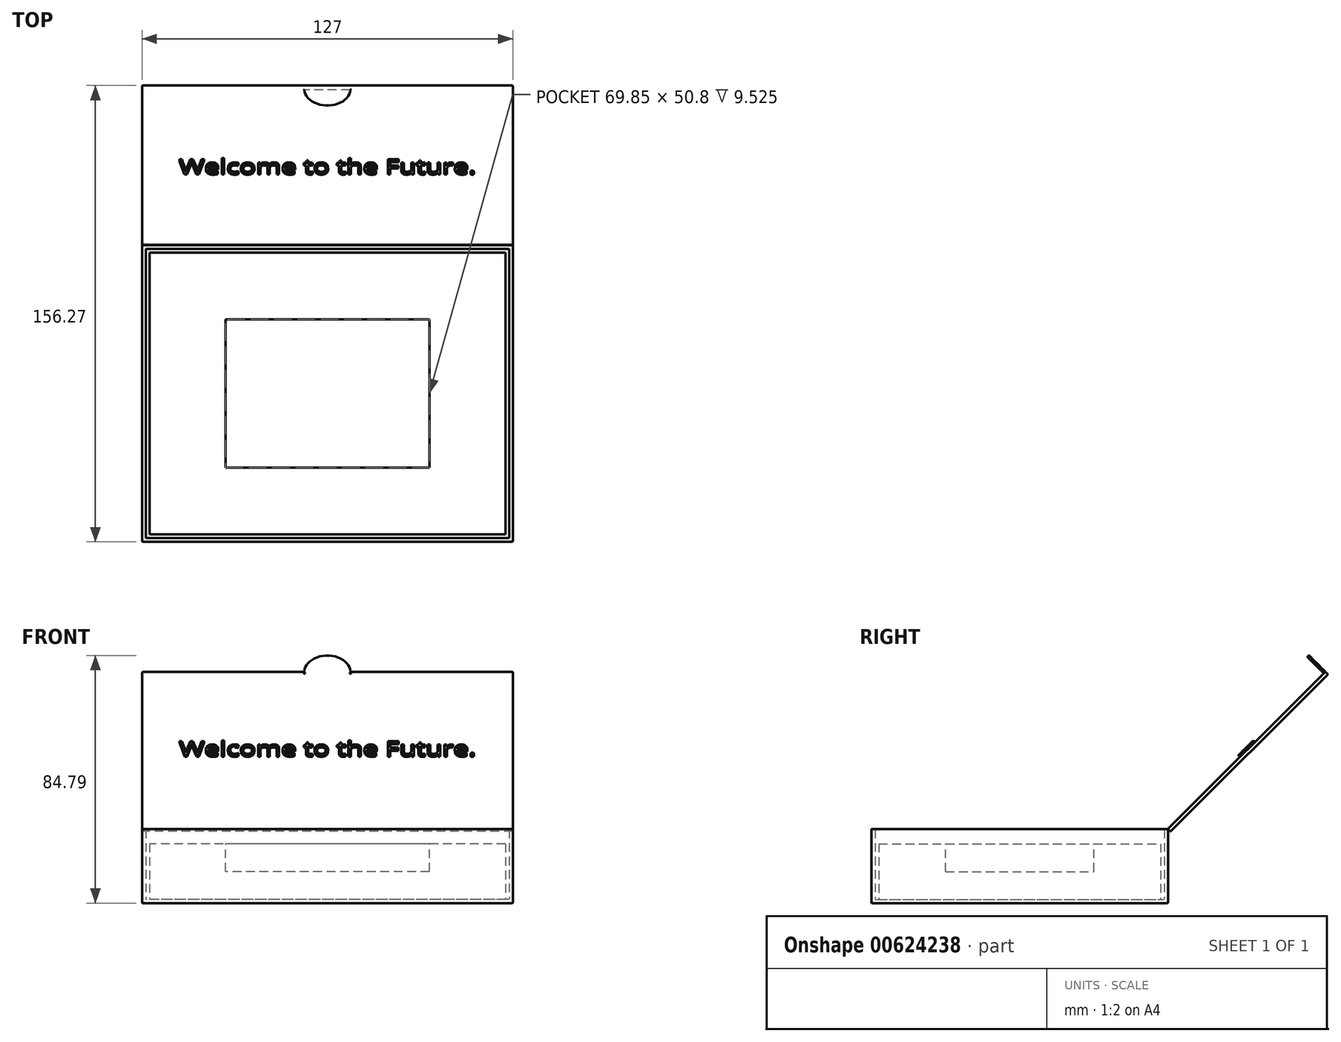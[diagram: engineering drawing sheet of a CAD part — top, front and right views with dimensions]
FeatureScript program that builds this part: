
annotation { "Feature Type Name" : "Feature", "Feature Type Description" : "" }
export const myFeature = defineFeature(function(context is Context, id is Id, definition is map)
    precondition{}
    {
        {
            var Q0;
            Q0=qCreatedBy(makeId("Top.planeOp"),FACE);
            var sketch = newSketch(context, id + "F0", { "sketchPlane" : qUnion([Q0])});
            skLineSegment(sketch, "E0.bottom", {"start": v(63.5, -50.8) * mm, "end": v(-63.5, -50.8) * mm});
            skLineSegment(sketch, "E0.top", {"start": v(63.5, 50.8) * mm, "end": v(-63.5, 50.8) * mm});
            skLineSegment(sketch, "E0.left", {"start": v(63.5, -50.8) * mm, "end": v(63.5, 50.8) * mm});
            skLineSegment(sketch, "E0.right", {"start": v(-63.5, -50.8) * mm, "end": v(-63.5, 50.8) * mm});
            skPoint(sketch, "E0.middle", {"position": v(0, 0) * mm});
            skSolve(sketch);
        }
        {
            var Q0;
            Q0 = qSketchRegion(id + "F0", true);
            extrude(context, id + "F1", {"entities" : qUnion([Q0]), "depth" : 25.4 * mm, "offsetDistance" : 25.4 * mm});
        }
        {
            var Q0;
            Q0=makeQuery(id+"F1.opExtrude","CAP_FACE",FACE,{"disambiguationData":[OSD([sQuery(id+"F0.wireOp",EDGE,"E0.bottom"),sQuery(id+"F0.wireOp",EDGE,"E0.top"),sQuery(id+"F0.wireOp",EDGE,"E0.left"),sQuery(id+"F0.wireOp",EDGE,"E0.right")])],"isStart":false});
            shell(context, id + "F2", {"entities" : qUnion([Q0]), "thickness" : 1.27 * mm});
        }
        {
            var Q0;
            Q0=qCreatedBy(makeId("Right.planeOp"),FACE);
            var sketch = newSketch(context, id + "F3", { "sketchPlane" : qUnion([Q0])});
            skLineSegment(sketch, "E1.0.2", {"start": v(50.8, 25.4) * mm, "end": v(-50.8, 25.4) * mm, "construction": true});
            skLineSegment(sketch, "E2", {"start": v(50.8, 25.4) * mm, "end": v(104.68, 79.28) * mm});
            skLineSegment(sketch, "E3.0", {"start": v(51.7, 24.5) * mm, "end": v(105.58, 78.38) * mm});
            skLineSegment(sketch, "E4", {"start": v(50.8, 25.4) * mm, "end": v(51.7, 24.5) * mm});
            skLineSegment(sketch, "E5", {"start": v(104.68, 79.28) * mm, "end": v(105.58, 78.38) * mm});
            skSolve(sketch);
        }
        {
            var Q0;
            Q0 = qSketchRegion(id + "F3", true);
            var Q1;
            Q1=makeQuery(id+"F1.opExtrude","SWEPT_FACE",FACE,{"disambiguationData":[OSD([sQuery(id+"F0.wireOp",EDGE,"E0.left")])]});
            var Q2;
            Q2=makeQuery(id+"F1.opExtrude","SWEPT_FACE",FACE,{"disambiguationData":[OSD([sQuery(id+"F0.wireOp",EDGE,"E0.right")])]});
            extrude(context, id + "F4", {"entities" : qUnion([Q0]), "endBound" : BoundingType.UP_TO_SURFACE, "depth" : 25.4 * mm, "endBoundEntityFace" : qUnion([Q1]), "offsetDistance" : 25.4 * mm, "hasSecondDirection" : true, "secondDirectionBound" : SecondDirectionBoundingType.UP_TO_SURFACE, "secondDirectionOppositeDirection" : true, "secondDirectionDepth" : 25.4 * mm, "secondDirectionBoundEntityFace" : qUnion([Q2])});
        }
        {
            var Q0;
            Q0=makeQuery(id+"F1.opExtrude","SWEPT_EDGE",EDGE,{"disambiguationData":[OSD([sQuery(id+"F0.wireOp",EDGE,"E0.bottom"),sQuery(id+"F0.wireOp",EDGE,"E0.left")])]});
            var Q1;
            Q1=makeQuery(id+"F1.opExtrude","SWEPT_EDGE",EDGE,{"disambiguationData":[OSD([sQuery(id+"F0.wireOp",EDGE,"E0.bottom"),sQuery(id+"F0.wireOp",EDGE,"E0.right")])]});
            var Q2;
            Q2=makeQuery(id+"F1.opExtrude","CAP_FACE",FACE,{"disambiguationData":[OSD([sQuery(id+"F0.wireOp",EDGE,"E0.bottom"),sQuery(id+"F0.wireOp",EDGE,"E0.top"),sQuery(id+"F0.wireOp",EDGE,"E0.left"),sQuery(id+"F0.wireOp",EDGE,"E0.right")])],"isStart":true});
            var Q3;
            Q3=makeQuery(id+"F2.opShell","OFFSET_FACE",FACE,{"disambiguationData":[OSD([sQuery(id+"F0.wireOp",EDGE,"E0.bottom"),sQuery(id+"F0.wireOp",EDGE,"E0.top"),sQuery(id+"F0.wireOp",EDGE,"E0.left"),sQuery(id+"F0.wireOp",EDGE,"E0.right")])]});
            var Q4;
            Q4=makeQuery(id+"F2.opShell","OFFSET_FACE",FACE,{"disambiguationData":[OSD([sQuery(id+"F0.wireOp",EDGE,"E0.bottom")])]});
            var Q5;
            Q5=makeQuery(id+"F2.opShell","OFFSET_FACE",FACE,{"disambiguationData":[OSD([sQuery(id+"F0.wireOp",EDGE,"E0.top")])]});
            var Q6;
            Q6=makeQuery(id+"F1.opExtrude","CAP_FACE",FACE,{"disambiguationData":[OSD([sQuery(id+"F0.wireOp",EDGE,"E0.bottom"),sQuery(id+"F0.wireOp",EDGE,"E0.top"),sQuery(id+"F0.wireOp",EDGE,"E0.left"),sQuery(id+"F0.wireOp",EDGE,"E0.right")])],"isStart":false});
            fillet(context, id + "F5", {"entities" : qUnion([Q0, Q1, Q2, Q3, Q4, Q5, Q6]), "radius" : 0.25 * mm, "tangentPropagation" : true, "allowEdgeOverflow" : false});
        }
        {
            var Q0;
            Q0=makeQuery(id+"F4.opExtrude","SWEPT_FACE",FACE,{"disambiguationData":[OSD([sQuery(id+"F3.wireOp",EDGE,"E5")])]});
            var sketch = newSketch(context, id + "F6", { "sketchPlane" : qUnion([Q0])});
            skArc(sketch, "E6", {"start": v(7.94, -17.96) * mm, "mid": v(0, -10.02) * mm, "end": v(-7.94, -17.96) * mm});
            skLineSegment(sketch, "E7", {"start": v(-7.94, -17.96) * mm, "end": v(7.94, -17.96) * mm});
            skSolve(sketch);
        }
        {
            var Q0;
            Q0 = qSketchRegion(id + "F6", true);
            extrude(context, id + "F7", {"entities" : qUnion([Q0]), "operationType" : NewBodyOperationType.ADD, "oppositeDirection" : true, "depth" : 0.76 * mm, "offsetDistance" : 25.4 * mm});
        }
        {
            var Q0;
            Q0=makeQuery(id+"F4.opExtrude","SWEPT_FACE",FACE,{"disambiguationData":[OSD([sQuery(id+"F3.wireOp",EDGE,"E3.0")])]});
            var Q1;
            Q1=makeQuery(id+"F4.opExtrude","SWEPT_FACE",FACE,{"disambiguationData":[OSD([sQuery(id+"F3.wireOp",EDGE,"E2")])]});
            var Q2;
            Q2=makeQuery(id+"F4.opExtrude","SWEPT_FACE",FACE,{"disambiguationData":[OSD([sQuery(id+"F3.wireOp",EDGE,"E5")])]});
            var Q3;
            Q3=makeQuery(id+"F7.opExtrude","CAP_EDGE",EDGE,{"disambiguationData":[OSD([sQuery(id+"F6.wireOp",EDGE,"E6")])],"isStart":false});
            fillet(context, id + "F8", {"entities" : qUnion([Q0, Q1, Q2, Q3]), "radius" : 0.25 * mm, "tangentPropagation" : true, "allowEdgeOverflow" : false});
        }
        {
            var Q0;
            Q0=makeQuery(id+"F4.opExtrude","SWEPT_FACE",FACE,{"disambiguationData":[OSD([sQuery(id+"F3.wireOp",EDGE,"E2")])]});
            var sketch = newSketch(context, id + "F9", { "sketchPlane" : qUnion([Q0])});
            skPoint(sketch, "E8", {"position": v(-63.25, 91.98) * mm});
            skPoint(sketch, "E9", {"position": v(0, 130.08) * mm});
            skText(sketch, "E10", { "text": "Welcome to the Future.", "fontName": "OpenSans-Regular.ttf"});
            const initialGuessF9  = {"E10": [-0.0508, 0.08892, 1, 0, 0.00671]};
            skSetInitialGuess(sketch, initialGuessF9);
            skSolve(sketch);
        }
        {
            var Q0;
            Q0=makeQuery(id+"F2.opShell","OFFSET_FACE",FACE,{"disambiguationData":[OSD([sQuery(id+"F0.wireOp",EDGE,"E0.bottom"),sQuery(id+"F0.wireOp",EDGE,"E0.top"),sQuery(id+"F0.wireOp",EDGE,"E0.left"),sQuery(id+"F0.wireOp",EDGE,"E0.right")])]});
            var sketch = newSketch(context, id + "F10", { "sketchPlane" : qUnion([Q0])});
            skLineSegment(sketch, "E11.0", {"start": v(60.96, 48.26) * mm, "end": v(-60.96, 48.26) * mm});
            skLineSegment(sketch, "E11.1", {"start": v(60.96, -48.26) * mm, "end": v(60.96, 48.26) * mm});
            skLineSegment(sketch, "E11.2", {"start": v(60.96, -48.26) * mm, "end": v(-60.96, -48.26) * mm});
            skLineSegment(sketch, "E11.3", {"start": v(-60.96, -48.26) * mm, "end": v(-60.96, 48.26) * mm});
            skSolve(sketch);
        }
        {
            var Q0;
            Q0 = qSketchRegion(id + "F10", true);
            extrude(context, id + "F11", {"entities" : qUnion([Q0]), "depth" : 19.05 * mm, "offsetDistance" : 25.4 * mm});
        }
        {
            var Q0;
            Q0=makeQuery(id+"F11.opExtrude","CAP_FACE",FACE,{"disambiguationData":[OSD([sQuery(id+"F10.wireOp",EDGE,"E11.0"),sQuery(id+"F10.wireOp",EDGE,"E11.1"),sQuery(id+"F10.wireOp",EDGE,"E11.2"),sQuery(id+"F10.wireOp",EDGE,"E11.3")])],"isStart":false});
            var sketch = newSketch(context, id + "F12", { "sketchPlane" : qUnion([Q0])});
            skLineSegment(sketch, "E12.bottom", {"start": v(34.93, -25.4) * mm, "end": v(-34.92, -25.4) * mm});
            skLineSegment(sketch, "E12.top", {"start": v(34.92, 25.4) * mm, "end": v(-34.93, 25.4) * mm});
            skLineSegment(sketch, "E12.left", {"start": v(34.93, -25.4) * mm, "end": v(34.92, 25.4) * mm});
            skLineSegment(sketch, "E12.right", {"start": v(-34.92, -25.4) * mm, "end": v(-34.93, 25.4) * mm});
            skPoint(sketch, "E12.middle", {"position": v(0, 0) * mm});
            skPoint(sketch, "E12.middle.positionSnap0", {"position": v(-60.96, 0) * mm});
            skPoint(sketch, "E12.middle.positionSnap1", {"position": v(0, 48.26) * mm});
            skPoint(sketch, "E12.centerSnap0", {"position": v(-60.96, 0) * mm});
            skPoint(sketch, "E12.centerSnap1", {"position": v(0, 48.26) * mm});
            skSolve(sketch);
        }
        {
            var Q0;
            Q0 = qSketchRegion(id + "F12", true);
            extrude(context, id + "F13", {"entities" : qUnion([Q0]), "operationType" : NewBodyOperationType.REMOVE, "oppositeDirection" : true, "depth" : 9.52 * mm, "offsetDistance" : 25.4 * mm});
        }
        {
            var Q0;
            Q0 = qSketchRegion(id + "F9", true);
            extrude(context, id + "F14", {"entities" : qUnion([Q0]), "depth" : 0.76 * mm, "offsetDistance" : 25.4 * mm, "hasDraft" : true, "draftAngle" : 3 * degree});
        }
    });
